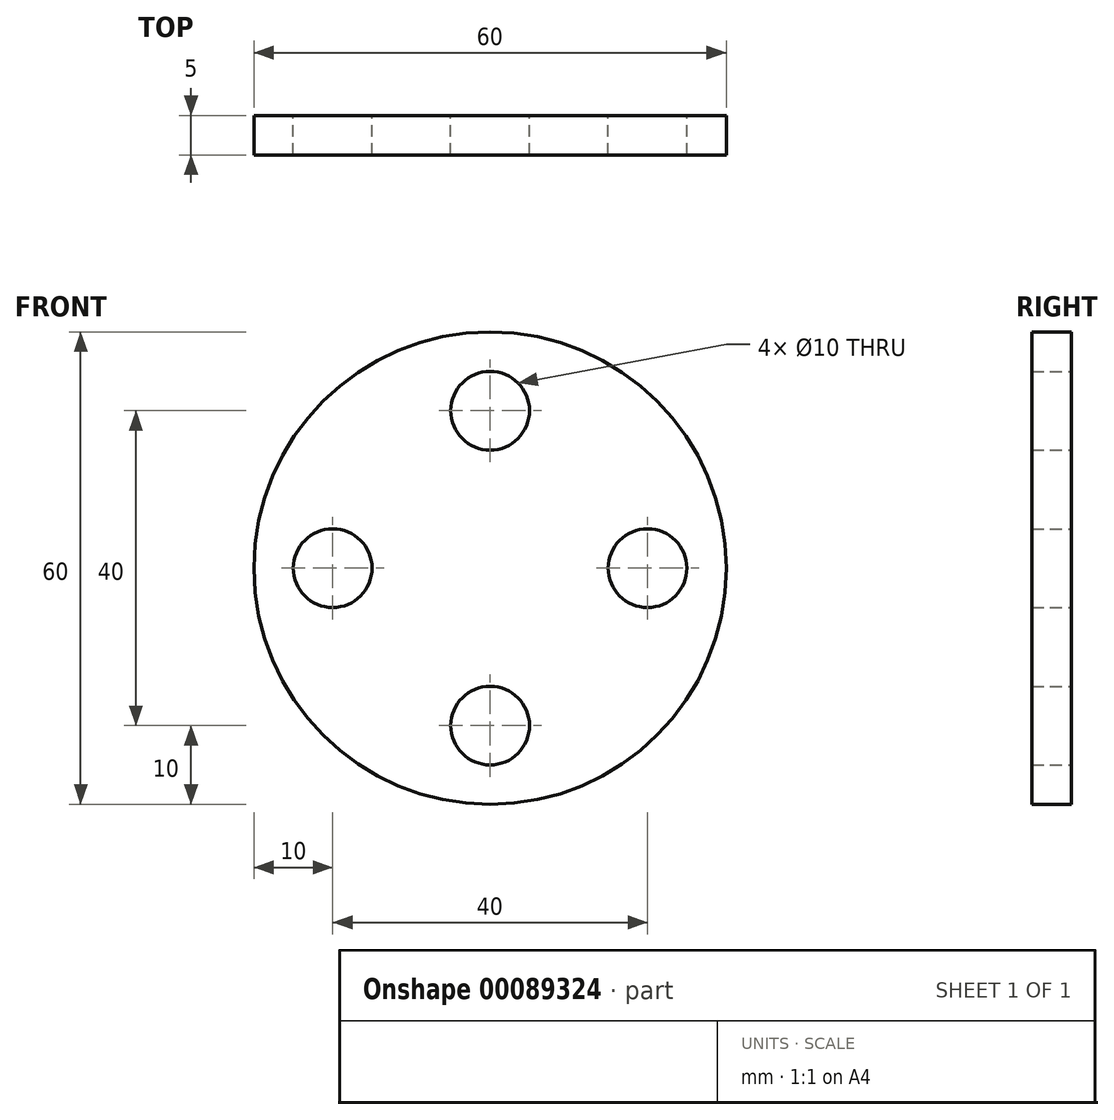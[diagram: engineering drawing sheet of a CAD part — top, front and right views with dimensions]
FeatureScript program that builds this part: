
annotation { "Feature Type Name" : "Feature", "Feature Type Description" : "" }
export const myFeature = defineFeature(function(context is Context, id is Id, definition is map)
    precondition{}
    {
        {
            var Q0;
            Q0=qCreatedBy(makeId("Front.planeOp"),FACE);
            var sketch = newSketch(context, id + "F0", { "sketchPlane" : qUnion([Q0])});
            skCircle(sketch, "E0", {"center": v(0, 0) * mm, "radius": 30 * mm});
            skCircle(sketch, "E1", {"center": v(0, 0) * mm, "radius": 20 * mm, "construction": true});
            skCircle(sketch, "E2", {"center": v(0, 20) * mm, "radius": 5 * mm});
            skCircle(sketch, "E3", {"center": v(-20, 0) * mm, "radius": 5 * mm});
            skCircle(sketch, "E4", {"center": v(0, -20) * mm, "radius": 5 * mm});
            skCircle(sketch, "E5", {"center": v(20, 0) * mm, "radius": 5 * mm});
            skSolve(sketch);
        }
        {
            var Q0;
            Q0 = qSketchRegion(id + "F0", true);
            extrude(context, id + "F1", {"entities" : qUnion([Q0]), "depth" : 5 * mm});
        }
    });
